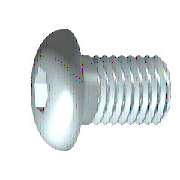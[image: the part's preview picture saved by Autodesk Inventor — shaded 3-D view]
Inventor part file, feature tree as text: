
AUTODESK INVENTOR PART (.ipt)
format: ipt  version: 2015 (Build 190159000, 159)  size: 191,488 bytes
history: native  units: mm (DEFAULTED — no unit token found)
features: sketch x2, extrude x1, plane x1, fillet x1
ambient origin geometry x7: Origin, YZ Plane, XY Plane, X Axis, Y Axis, Z Axis, Center Point
bodies: Solid1 (feature_tree), Body (feature_tree)
feature tree (5):
  extrude  "Slot"  Depth=1.8542mm
  plane  "Work Plane1"
  fillet  "Fillet2"  Radius=1.8542mm
  sketch  "Sketch1"  dims[d1=14.28476mm d2=1.59014mm d3=1.8542mm]
  sketch  "Sketch2"  dims[d4=1.1176mm d5=60.0deg d6=3.5052mm d7=3.5052mm d8=2.287693mm d9=6.6548mm d10=90.0deg d11=10.0mm d12=0.0mm d13=14.28476mm d14=0.0mm d15=0.486918mm d16=0.486918mm d17=1.6002mm d19=0.0mm d26=15.875mm d27=45.0deg d28=0.0mm d29=0.0mm d30=0.1mm]
